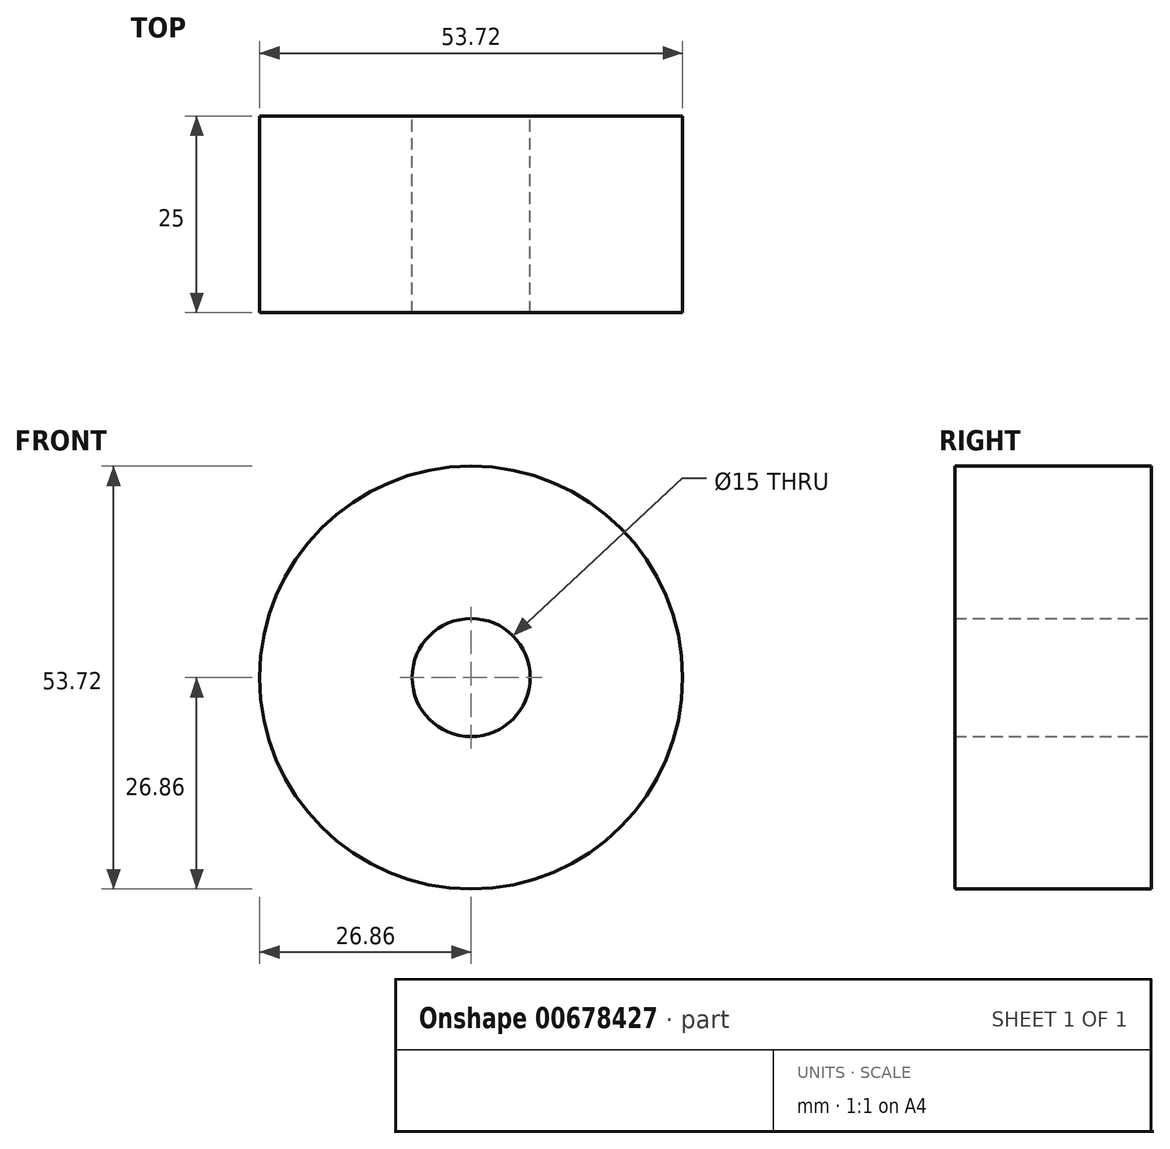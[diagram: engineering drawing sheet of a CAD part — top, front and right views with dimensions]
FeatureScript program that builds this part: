
annotation { "Feature Type Name" : "Feature", "Feature Type Description" : "" }
export const myFeature = defineFeature(function(context is Context, id is Id, definition is map)
    precondition{}
    {
        {
            var Q0;
            Q0=qCreatedBy(makeId("Front.planeOp"),FACE);
            var sketch = newSketch(context, id + "F0", { "sketchPlane" : qUnion([Q0])});
            skCircle(sketch, "E0", {"center": v(0, 0) * mm, "radius": 26.86 * mm});
            skCircle(sketch, "E1", {"center": v(0, 0) * mm, "radius": 29.34 * mm, "construction": true});
            skCircle(sketch, "E2", {"center": v(0, 0) * mm, "radius": 31.75 * mm, "construction": true});
            skLineSegment(sketch, "E3", {"start": v(0, 0) * mm, "end": v(0, 101.1) * mm, "construction": true});
            skLineSegment(sketch, "E4", {"start": v(0, 0) * mm, "end": v(-6.42, 98) * mm, "construction": true});
            skLineSegment(sketch, "E5", {"start": v(0, 29.34) * mm, "end": v(-48.84, 29.34) * mm, "construction": true});
            skLineSegment(sketch, "E6", {"start": v(0, 29.34) * mm, "end": v(-46.23, 12.51) * mm, "construction": true});
            skCircle(sketch, "E7", {"center": v(0, 0) * mm, "radius": 27.57 * mm, "construction": true});
            skCircle(sketch, "E8", {"center": v(0, 29.34) * mm, "radius": 14.6 * mm, "construction": true});
            skCircle(sketch, "E9", {"center": v(-13.72, 24.34) * mm, "radius": 14.6 * mm, "construction": true});
            skArc(sketch, "E10.MirrorCS", {"start": v(-5.88, 31.19) * mm, "mid": v(-5.02, 33.84) * mm, "end": v(-3.67, 36.28) * mm});
            skArc(sketch, "E11.MirrorCS", {"start": v(-6.1, 26.16) * mm, "mid": v(-6.22, 28.68) * mm, "end": v(-5.88, 31.19) * mm});
            skArc(sketch, "E12.MirrorCS", {"start": v(1.76, 31.7) * mm, "mid": v(0.56, 34.2) * mm, "end": v(-1.1, 36.45) * mm});
            skArc(sketch, "E13.MirrorCS", {"start": v(2.64, 26.73) * mm, "mid": v(2.43, 29.25) * mm, "end": v(1.76, 31.7) * mm});
            skArc(sketch, "E14", {"start": v(-1.1, 36.45) * mm, "mid": v(-2.41, 36.8) * mm, "end": v(-3.67, 36.28) * mm});
            skCircle(sketch, "E15", {"center": v(0, 0) * mm, "radius": 7.5 * mm});
            skSolve(sketch);
        }
        {
            var Q0;
            {var subQ0=sQuery(id+"F0.wireOp",EDGE,"E0");var subQ1=makeQuery(id+"F0.imprint","INTERSECT",VERTEX,{"derivedFrom":[subQ0,sQuery(id+"F0.wireOp",EDGE,"E11.MirrorCS")]});Q0=makeQuery(id+"F0.imprint","IMPRINT",FACE,{"disambiguationData":[TD([[makeQuery(id+"F0.imprint","IMPRINT",EDGE,{"disambiguationData":[TD([[subQ1,1.0]])],"derivedFrom":subQ0}),1.0]])]});}
            var Q1;
            Q1=makeQuery(id+"F0.imprint","IMPRINT",FACE,{"disambiguationData":[TD([[makeQuery(id+"F0.imprint","IMPRINT",EDGE,{"derivedFrom":sQuery(id+"F0.wireOp",EDGE,"E10.MirrorCS")}),-1.0]])]});
            extrude(context, id + "F1", {"entities" : qUnion([Q0, Q1]), "depth" : 25 * mm, "offsetDistance" : 25 * mm});
        }
        {
            var Q0;
            Q0=makeQuery(id+"F1.opExtrude","SWEPT_BODY",BODY,{"disambiguationData":[OSD([sQuery(id+"F0.wireOp",EDGE,"E0"),sQuery(id+"F0.wireOp",EDGE,"6b7d58f2-b462-40b3-960e-51561fa49fb0.MirrorCS"),sQuery(id+"F0.wireOp",EDGE,"33852964-fe23-4fde-b8e8-dc38bec01309.MirrorCS"),sQuery(id+"F0.wireOp",EDGE,"0bdbd0b5-8b60-4639-95da-5647509a0f890.MirrorCS"),sQuery(id+"F0.wireOp",EDGE,"06a8ee0e-aa0b-447a-9080-d4317896a0e40.MirrorCS"),sQuery(id+"F0.wireOp",EDGE,"TU7oJ0Q2-bCSg-hST1-LLmd-DcQbNWx1LKyx")])]});
            var Q1;
            Q1=makeQuery(id+"F1.opExtrude","SWEPT_FACE",FACE,{"disambiguationData":[OSD([sQuery(id+"F0.wireOp",EDGE,"E0")])]});
            circularPattern(context, id + "F2", {"operationType" : NewBodyOperationType.ADD, "entities" : qUnion([Q0]), "axis" : qUnion([Q1]), "angle" : 360 * degree, "instanceCount" : 12, "equalSpace" : true});
        }
    });
